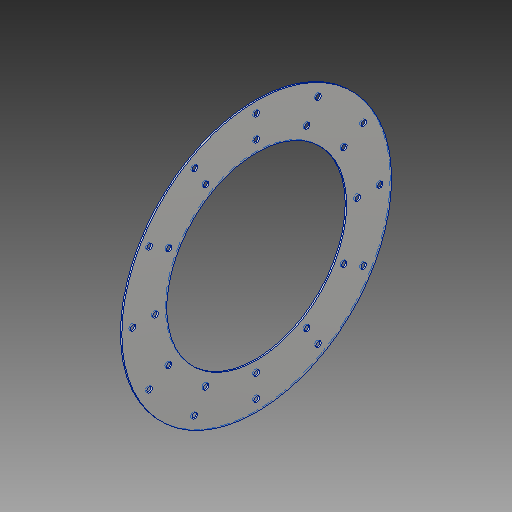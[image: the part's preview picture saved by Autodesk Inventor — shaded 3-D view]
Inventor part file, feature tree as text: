
AUTODESK INVENTOR PART (.ipt)
format: ipt  version: 2019 (Build 230136000, 136)  size: 129,024 bytes
history: native  units: in
note: dims shown in document units (in); Inventor stores cm internally (conversion verified against a paired STEP export)
features: extrude x2, sketch x2
ambient origin geometry x8: Origin, YZ Plane, XZ Plane, XY Plane, X Axis, Y Axis, Z Axis, Center Point
bodies: Solid1 (feature_tree)
feature tree (4):
  extrude  "Extrusion1"  Depth=0.5in
  extrude  "Extrusion2"  Depth=0.0625in
  sketch  "Sketch1"  dims[d0=12.0in d1=0.5in]
  sketch  "Sketch2"  dims[d2=1.0in d3=0.25in d4=4.7244in d6=360.0deg d8=0.0625in d9=0.0in d10=8.0in d11=1.0in d12=0.0in]
